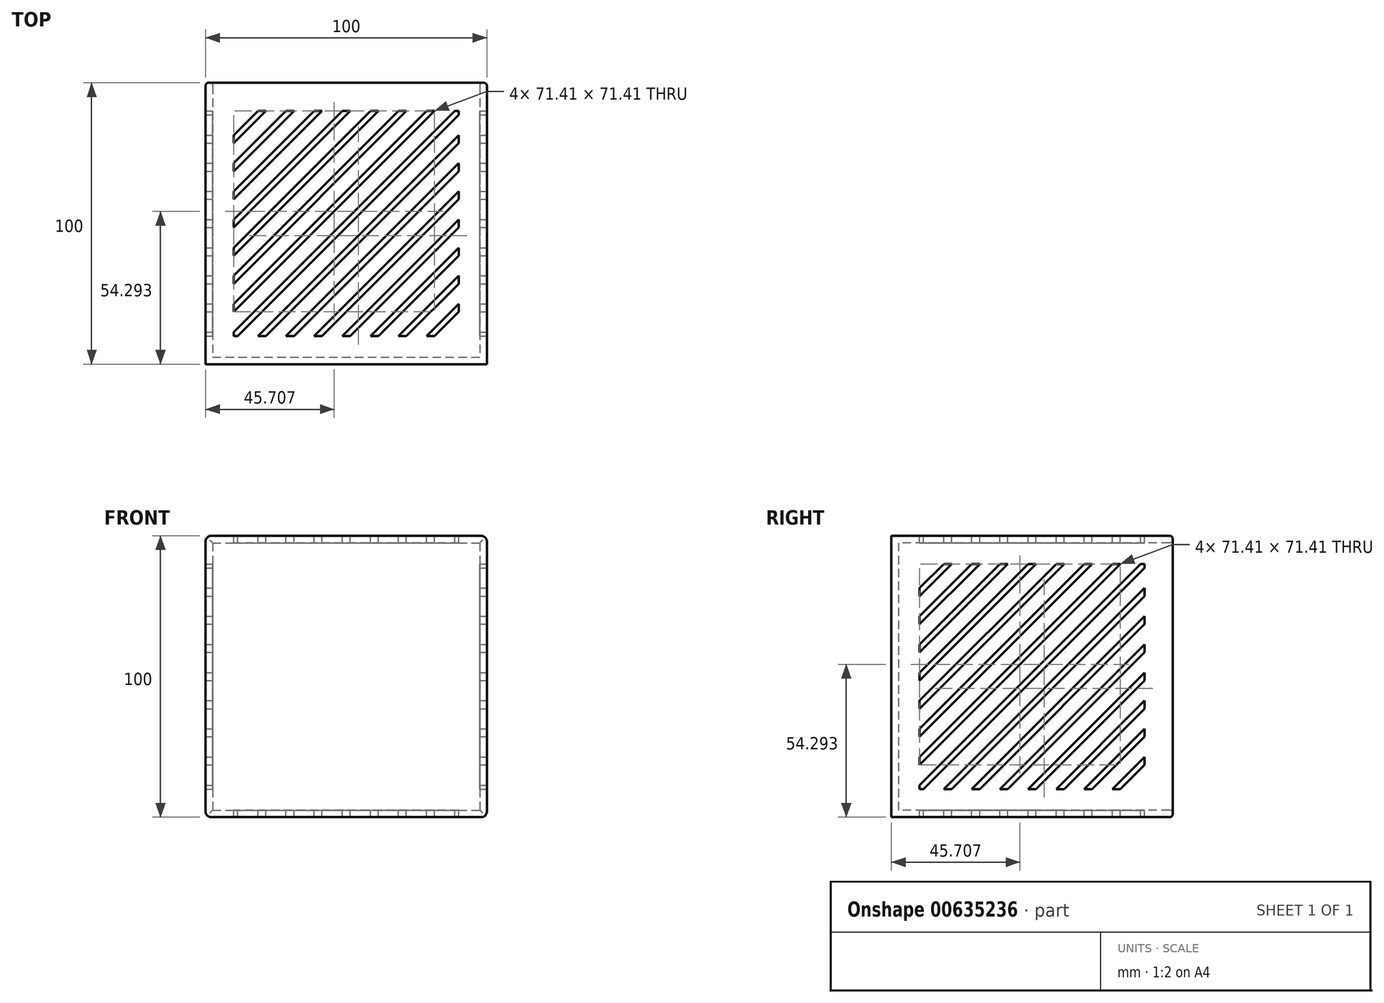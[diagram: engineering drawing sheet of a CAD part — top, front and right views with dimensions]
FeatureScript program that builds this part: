
annotation { "Feature Type Name" : "Feature", "Feature Type Description" : "" }
export const myFeature = defineFeature(function(context is Context, id is Id, definition is map)
    precondition{}
    {
        {
            var Q0;
            Q0=qCreatedBy(makeId("Top.planeOp"),FACE);
            var sketch = newSketch(context, id + "F0", { "sketchPlane" : qUnion([Q0])});
            skLineSegment(sketch, "E0.bottom", {"start": v(-50, 50) * mm, "end": v(50, 50) * mm});
            skLineSegment(sketch, "E0.top", {"start": v(-50, -50) * mm, "end": v(50, -50) * mm});
            skLineSegment(sketch, "E0.left", {"start": v(-50, 50) * mm, "end": v(-50, -50) * mm});
            skLineSegment(sketch, "E0.right", {"start": v(50, 50) * mm, "end": v(50, -50) * mm});
            skLineSegment(sketch, "E1", {"start": v(-30, 50) * mm, "end": v(-30, -50) * mm, "construction": true});
            skLineSegment(sketch, "E2", {"start": v(-20, 50) * mm, "end": v(-20, -50) * mm, "construction": true});
            skLineSegment(sketch, "E3", {"start": v(-10, 50) * mm, "end": v(-10, -50) * mm, "construction": true});
            skLineSegment(sketch, "E4", {"start": v(10, 50) * mm, "end": v(10, -50) * mm, "construction": true});
            skLineSegment(sketch, "E5", {"start": v(0, 50) * mm, "end": v(0, -50) * mm, "construction": true});
            skLineSegment(sketch, "E6", {"start": v(20, 50) * mm, "end": v(20, -50) * mm, "construction": true});
            skLineSegment(sketch, "E7", {"start": v(30, 50) * mm, "end": v(30, -50) * mm, "construction": true});
            skLineSegment(sketch, "E8", {"start": v(40, 50) * mm, "end": v(40, -50) * mm, "construction": true});
            skLineSegment(sketch, "E9", {"start": v(-40, 50) * mm, "end": v(-40, -50) * mm, "construction": true});
            skLineSegment(sketch, "E10", {"start": v(-50, 40) * mm, "end": v(50, 40) * mm, "construction": true});
            skLineSegment(sketch, "E11", {"start": v(-50, 30) * mm, "end": v(50, 30) * mm, "construction": true});
            skLineSegment(sketch, "E12", {"start": v(-50, 20) * mm, "end": v(50, 20) * mm, "construction": true});
            skLineSegment(sketch, "E13", {"start": v(-50, 10) * mm, "end": v(50, 10) * mm, "construction": true});
            skLineSegment(sketch, "E14", {"start": v(-50, -40) * mm, "end": v(50, -40) * mm, "construction": true});
            skLineSegment(sketch, "E15", {"start": v(50, -30) * mm, "end": v(-50, -30) * mm, "construction": true});
            skLineSegment(sketch, "E16", {"start": v(-50, -20) * mm, "end": v(50, -20) * mm, "construction": true});
            skLineSegment(sketch, "E17", {"start": v(-50, -10) * mm, "end": v(50, -10) * mm, "construction": true});
            skLineSegment(sketch, "E18", {"start": v(-50, 0) * mm, "end": v(50, 0) * mm, "construction": true});
            skSolve(sketch);
        }
        {
            var Q0;
            Q0=makeQuery(id+"F0.imprint","IMPRINT",FACE,{"disambiguationData":[TD([[makeQuery(id+"F0.imprint","IMPRINT",EDGE,{"derivedFrom":sQuery(id+"F0.wireOp",EDGE,"E0.bottom")}),-1.0]])]});
            extrude(context, id + "F1", {"entities" : qUnion([Q0]), "depth" : 100 * mm, "offsetDistance" : 25 * mm});
        }
        {
            var Q0;
            Q0=makeQuery(id+"F1.opExtrude","CAP_FACE",FACE,{"disambiguationData":[OSD([sQuery(id+"F0.wireOp",EDGE,"E0.bottom"),sQuery(id+"F0.wireOp",EDGE,"E0.top"),sQuery(id+"F0.wireOp",EDGE,"E0.left"),sQuery(id+"F0.wireOp",EDGE,"E0.right")])],"isStart":false});
            var sketch = newSketch(context, id + "F2", { "sketchPlane" : qUnion([Q0])});
            skLineSegment(sketch, "E19.bottom", {"start": v(-50, 50) * mm, "end": v(50, 50) * mm});
            skLineSegment(sketch, "E19.top", {"start": v(-50, -50) * mm, "end": v(50, -50) * mm});
            skLineSegment(sketch, "E19.left", {"start": v(-50, 50) * mm, "end": v(-50, -50) * mm});
            skLineSegment(sketch, "E19.right", {"start": v(50, 50) * mm, "end": v(50, -50) * mm});
            skLineSegment(sketch, "E20", {"start": v(40, 40) * mm, "end": v(40, -40) * mm});
            skLineSegment(sketch, "E21", {"start": v(-40, 40) * mm, "end": v(-40, -40) * mm});
            skLineSegment(sketch, "E22", {"start": v(-40, 40) * mm, "end": v(40, 40) * mm});
            skLineSegment(sketch, "E23", {"start": v(-40, -40) * mm, "end": v(40, -40) * mm});
            skLineSegment(sketch, "E24", {"start": v(-40, 31.41) * mm, "end": v(-31.41, 40) * mm});
            skLineSegment(sketch, "E25", {"start": v(-40, 21.41) * mm, "end": v(-21.41, 40) * mm});
            skLineSegment(sketch, "E26", {"start": v(-40, 11.41) * mm, "end": v(-11.41, 40) * mm});
            skLineSegment(sketch, "E27", {"start": v(-40, 28.59) * mm, "end": v(-28.59, 40) * mm});
            skLineSegment(sketch, "E28", {"start": v(-40, 18.59) * mm, "end": v(-18.59, 40) * mm});
            skLineSegment(sketch, "E29", {"start": v(-40, 8.59) * mm, "end": v(-8.59, 40) * mm});
            skLineSegment(sketch, "E30", {"start": v(-40, 1.41) * mm, "end": v(-1.41, 40) * mm});
            skLineSegment(sketch, "E31", {"start": v(-40, -1.41) * mm, "end": v(1.41, 40) * mm});
            skLineSegment(sketch, "E32", {"start": v(-40, -8.59) * mm, "end": v(8.59, 40) * mm});
            skLineSegment(sketch, "E33", {"start": v(-40, -11.41) * mm, "end": v(11.41, 40) * mm});
            skLineSegment(sketch, "E34", {"start": v(-40, -18.59) * mm, "end": v(18.59, 40) * mm});
            skLineSegment(sketch, "E35", {"start": v(-40, -21.41) * mm, "end": v(21.41, 40) * mm});
            skLineSegment(sketch, "E36", {"start": v(-40, -28.59) * mm, "end": v(28.59, 40) * mm});
            skLineSegment(sketch, "E37", {"start": v(31.41, 40) * mm, "end": v(-40, -31.41) * mm});
            skLineSegment(sketch, "E38", {"start": v(-40, -38.59) * mm, "end": v(38.59, 40) * mm});
            skLineSegment(sketch, "E39", {"start": v(-38.59, -40) * mm, "end": v(40, 38.59) * mm});
            skLineSegment(sketch, "E40", {"start": v(-31.41, -40) * mm, "end": v(40, 31.41) * mm});
            skLineSegment(sketch, "E41", {"start": v(-28.59, -40) * mm, "end": v(40, 28.59) * mm});
            skLineSegment(sketch, "E42", {"start": v(-21.41, -40) * mm, "end": v(40, 21.41) * mm});
            skLineSegment(sketch, "E43", {"start": v(-18.59, -40) * mm, "end": v(40, 18.59) * mm});
            skLineSegment(sketch, "E44", {"start": v(-11.41, -40) * mm, "end": v(40, 11.41) * mm});
            skLineSegment(sketch, "E45", {"start": v(40, 8.59) * mm, "end": v(-8.59, -40) * mm});
            skLineSegment(sketch, "E46", {"start": v(-1.41, -40) * mm, "end": v(40, 1.41) * mm});
            skLineSegment(sketch, "E47", {"start": v(40, -1.41) * mm, "end": v(1.41, -40) * mm});
            skLineSegment(sketch, "E48", {"start": v(11.41, -40) * mm, "end": v(40, -11.41) * mm});
            skLineSegment(sketch, "E49", {"start": v(8.59, -40) * mm, "end": v(40, -8.59) * mm});
            skLineSegment(sketch, "E50", {"start": v(18.59, -40) * mm, "end": v(40, -18.59) * mm});
            skLineSegment(sketch, "E51", {"start": v(21.41, -40) * mm, "end": v(40, -21.41) * mm});
            skLineSegment(sketch, "E52", {"start": v(31.41, -40) * mm, "end": v(40, -31.41) * mm});
            skLineSegment(sketch, "E53", {"start": v(40, -28.59) * mm, "end": v(28.59, -40) * mm});
            skPoint(sketch, "E54.orphan", {"position": v(-50, 40) * mm});
            skPoint(sketch, "E55.orphan", {"position": v(-40, 50) * mm});
            skPoint(sketch, "E56.orphan", {"position": v(-50, 0) * mm});
            skPoint(sketch, "E57.orphan", {"position": v(-50, -40) * mm});
            skPoint(sketch, "E58.orphan", {"position": v(-40, -50) * mm});
            skPoint(sketch, "E59.orphan", {"position": v(40, -50) * mm});
            skPoint(sketch, "E60.orphan", {"position": v(50, -40) * mm});
            skPoint(sketch, "E61.orphan", {"position": v(50, 40) * mm});
            skPoint(sketch, "E62.orphan", {"position": v(40, 50) * mm});
            skSolve(sketch);
        }
        {
            var Q0;
            Q0=makeQuery(id+"F1.opExtrude","SWEPT_FACE",FACE,{"disambiguationData":[OSD([sQuery(id+"F0.wireOp",EDGE,"E0.bottom")])]});
            shell(context, id + "F3", {"entities" : qUnion([Q0]), "thickness" : 2.5 * mm});
        }
        {
            var Q0;
            {var subQ0=sQuery(id+"F2.wireOp",EDGE,"E24");Q0=makeQuery(id+"F2.imprint","IMPRINT",FACE,{"disambiguationData":[TD([[makeQuery(id+"F2.imprint","IMPRINT",EDGE,{"derivedFrom":subQ0}),-1.0]])]});}
            var Q1;
            {var subQ0=sQuery(id+"F2.wireOp",EDGE,"E25");Q1=makeQuery(id+"F2.imprint","IMPRINT",FACE,{"disambiguationData":[TD([[makeQuery(id+"F2.imprint","IMPRINT",EDGE,{"derivedFrom":subQ0}),-1.0]])]});}
            var Q2;
            {var subQ0=sQuery(id+"F2.wireOp",EDGE,"E26");Q2=makeQuery(id+"F2.imprint","IMPRINT",FACE,{"disambiguationData":[TD([[makeQuery(id+"F2.imprint","IMPRINT",EDGE,{"derivedFrom":subQ0}),-1.0]])]});}
            var Q3;
            {var subQ0=sQuery(id+"F2.wireOp",EDGE,"E30");Q3=makeQuery(id+"F2.imprint","IMPRINT",FACE,{"disambiguationData":[TD([[makeQuery(id+"F2.imprint","IMPRINT",EDGE,{"derivedFrom":subQ0}),-1.0]])]});}
            var Q4;
            {var subQ0=sQuery(id+"F2.wireOp",EDGE,"E32");Q4=makeQuery(id+"F2.imprint","IMPRINT",FACE,{"disambiguationData":[TD([[makeQuery(id+"F2.imprint","IMPRINT",EDGE,{"derivedFrom":subQ0}),-1.0]])]});}
            var Q5;
            {var subQ0=sQuery(id+"F2.wireOp",EDGE,"E34");Q5=makeQuery(id+"F2.imprint","IMPRINT",FACE,{"disambiguationData":[TD([[makeQuery(id+"F2.imprint","IMPRINT",EDGE,{"derivedFrom":subQ0}),-1.0]])]});}
            var Q6;
            {var subQ0=sQuery(id+"F2.wireOp",EDGE,"E36");Q6=makeQuery(id+"F2.imprint","IMPRINT",FACE,{"disambiguationData":[TD([[makeQuery(id+"F2.imprint","IMPRINT",EDGE,{"derivedFrom":subQ0}),-1.0]])]});}
            var Q7;
            {var subQ7=sQuery(id+"F2.wireOp",EDGE,"E38");Q7=makeQuery(id+"F2.imprint","IMPRINT",FACE,{"disambiguationData":[TD([[makeQuery(id+"F2.imprint","IMPRINT",EDGE,{"derivedFrom":subQ7}),-1.0]])]});}
            var Q8;
            {var subQ0=sQuery(id+"F2.wireOp",EDGE,"E40");Q8=makeQuery(id+"F2.imprint","IMPRINT",FACE,{"disambiguationData":[TD([[makeQuery(id+"F2.imprint","IMPRINT",EDGE,{"derivedFrom":subQ0}),-1.0]])]});}
            var Q9;
            {var subQ0=sQuery(id+"F2.wireOp",EDGE,"E42");Q9=makeQuery(id+"F2.imprint","IMPRINT",FACE,{"disambiguationData":[TD([[makeQuery(id+"F2.imprint","IMPRINT",EDGE,{"derivedFrom":subQ0}),-1.0]])]});}
            var Q10;
            {var subQ0=sQuery(id+"F2.wireOp",EDGE,"E44");Q10=makeQuery(id+"F2.imprint","IMPRINT",FACE,{"disambiguationData":[TD([[makeQuery(id+"F2.imprint","IMPRINT",EDGE,{"derivedFrom":subQ0}),-1.0]])]});}
            var Q11;
            {var subQ0=sQuery(id+"F2.wireOp",EDGE,"E46");Q11=makeQuery(id+"F2.imprint","IMPRINT",FACE,{"disambiguationData":[TD([[makeQuery(id+"F2.imprint","IMPRINT",EDGE,{"derivedFrom":subQ0}),-1.0]])]});}
            var Q12;
            {var subQ0=sQuery(id+"F2.wireOp",EDGE,"E48");Q12=makeQuery(id+"F2.imprint","IMPRINT",FACE,{"disambiguationData":[TD([[makeQuery(id+"F2.imprint","IMPRINT",EDGE,{"derivedFrom":subQ0}),1.0]])]});}
            var Q13;
            {var subQ0=sQuery(id+"F2.wireOp",EDGE,"E50");Q13=makeQuery(id+"F2.imprint","IMPRINT",FACE,{"disambiguationData":[TD([[makeQuery(id+"F2.imprint","IMPRINT",EDGE,{"derivedFrom":subQ0}),-1.0]])]});}
            var Q14;
            {var subQ0=sQuery(id+"F2.wireOp",EDGE,"E52");Q14=makeQuery(id+"F2.imprint","IMPRINT",FACE,{"disambiguationData":[TD([[makeQuery(id+"F2.imprint","IMPRINT",EDGE,{"derivedFrom":subQ0}),1.0]])]});}
            extrude(context, id + "F4", {"entities" : qUnion([Q0, Q1, Q2, Q3, Q4, Q5, Q6, Q7, Q8, Q9, Q10, Q11, Q12, Q13, Q14]), "operationType" : NewBodyOperationType.REMOVE, "oppositeDirection" : true, "depth" : 102 * mm, "offsetDistance" : 25 * mm});
        }
        {
            var Q0;
            Q0=makeQuery(id+"F1.opExtrude","SWEPT_FACE",FACE,{"disambiguationData":[OSD([sQuery(id+"F0.wireOp",EDGE,"E0.right")])]});
            var sketch = newSketch(context, id + "F5", { "sketchPlane" : qUnion([Q0])});
            skLineSegment(sketch, "E63.bottom", {"start": v(-50, 100) * mm, "end": v(50, 100) * mm});
            skLineSegment(sketch, "E63.top", {"start": v(-50, 0) * mm, "end": v(50, 0) * mm});
            skLineSegment(sketch, "E63.left", {"start": v(-50, 100) * mm, "end": v(-50, 0) * mm});
            skLineSegment(sketch, "E63.right", {"start": v(50, 100) * mm, "end": v(50, 0) * mm});
            skLineSegment(sketch, "E64", {"start": v(-30, 100) * mm, "end": v(-30, 0) * mm, "construction": true});
            skLineSegment(sketch, "E65", {"start": v(-20, 100) * mm, "end": v(-20, 0) * mm, "construction": true});
            skLineSegment(sketch, "E66", {"start": v(-10, 100) * mm, "end": v(-10, 0) * mm, "construction": true});
            skLineSegment(sketch, "E67", {"start": v(10, 100) * mm, "end": v(10, 0) * mm, "construction": true});
            skLineSegment(sketch, "E68", {"start": v(0, 100) * mm, "end": v(0, 0) * mm, "construction": true});
            skLineSegment(sketch, "E69", {"start": v(20, 100) * mm, "end": v(20, 0) * mm, "construction": true});
            skLineSegment(sketch, "E70", {"start": v(30, 100) * mm, "end": v(30, 0) * mm, "construction": true});
            skLineSegment(sketch, "E71", {"start": v(40, 100) * mm, "end": v(40, 0) * mm});
            skLineSegment(sketch, "E72", {"start": v(-40, 90) * mm, "end": v(-40, 0) * mm});
            skLineSegment(sketch, "E73", {"start": v(-40, 90) * mm, "end": v(50, 90) * mm});
            skLineSegment(sketch, "E74", {"start": v(-50, 80) * mm, "end": v(50, 80) * mm, "construction": true});
            skLineSegment(sketch, "E75", {"start": v(-50, 70) * mm, "end": v(50, 70) * mm, "construction": true});
            skLineSegment(sketch, "E76", {"start": v(-50, 60) * mm, "end": v(50, 60) * mm, "construction": true});
            skLineSegment(sketch, "E77", {"start": v(-50, 10) * mm, "end": v(50, 10) * mm});
            skLineSegment(sketch, "E78", {"start": v(50, 20) * mm, "end": v(-50, 20) * mm, "construction": true});
            skLineSegment(sketch, "E79", {"start": v(-50, 30) * mm, "end": v(50, 30) * mm, "construction": true});
            skLineSegment(sketch, "E80", {"start": v(-50, 40) * mm, "end": v(50, 40) * mm, "construction": true});
            skLineSegment(sketch, "E81", {"start": v(-50, 50) * mm, "end": v(50, 50) * mm, "construction": true});
            skLineSegment(sketch, "E82", {"start": v(-40, 81.41) * mm, "end": v(-31.41, 90) * mm});
            skLineSegment(sketch, "E83", {"start": v(-40, 71.41) * mm, "end": v(-21.41, 90) * mm});
            skLineSegment(sketch, "E84", {"start": v(-40, 61.41) * mm, "end": v(-11.41, 90) * mm});
            skLineSegment(sketch, "E85", {"start": v(-40, 78.59) * mm, "end": v(-28.59, 90) * mm});
            skLineSegment(sketch, "E86", {"start": v(-40, 68.59) * mm, "end": v(-18.59, 90) * mm});
            skLineSegment(sketch, "E87", {"start": v(-40, 58.59) * mm, "end": v(-8.59, 90) * mm});
            skLineSegment(sketch, "E88", {"start": v(-40, 51.41) * mm, "end": v(-1.41, 90) * mm});
            skLineSegment(sketch, "E89", {"start": v(-40, 48.59) * mm, "end": v(1.41, 90) * mm});
            skLineSegment(sketch, "E90", {"start": v(-40, 41.41) * mm, "end": v(8.59, 90) * mm});
            skLineSegment(sketch, "E91", {"start": v(-40, 38.59) * mm, "end": v(11.41, 90) * mm});
            skLineSegment(sketch, "E92", {"start": v(-40, 31.41) * mm, "end": v(18.59, 90) * mm});
            skLineSegment(sketch, "E93", {"start": v(-40, 28.59) * mm, "end": v(21.41, 90) * mm});
            skLineSegment(sketch, "E94", {"start": v(-40, 21.41) * mm, "end": v(28.59, 90) * mm});
            skLineSegment(sketch, "E95", {"start": v(31.41, 90) * mm, "end": v(-40, 18.59) * mm});
            skLineSegment(sketch, "E96", {"start": v(-40, 11.41) * mm, "end": v(38.59, 90) * mm});
            skLineSegment(sketch, "E97", {"start": v(-38.59, 10) * mm, "end": v(40, 88.59) * mm});
            skLineSegment(sketch, "E98", {"start": v(-31.41, 10) * mm, "end": v(40, 81.41) * mm});
            skLineSegment(sketch, "E99", {"start": v(-28.59, 10) * mm, "end": v(40, 78.59) * mm});
            skLineSegment(sketch, "E100", {"start": v(-21.41, 10) * mm, "end": v(40, 71.41) * mm});
            skLineSegment(sketch, "E101", {"start": v(-18.59, 10) * mm, "end": v(40, 68.59) * mm});
            skLineSegment(sketch, "E102", {"start": v(-11.41, 10) * mm, "end": v(40, 61.41) * mm});
            skLineSegment(sketch, "E103", {"start": v(40, 58.59) * mm, "end": v(-8.59, 10) * mm});
            skLineSegment(sketch, "E104", {"start": v(-1.41, 10) * mm, "end": v(40, 51.41) * mm});
            skLineSegment(sketch, "E105", {"start": v(40, 48.59) * mm, "end": v(1.41, 10) * mm});
            skLineSegment(sketch, "E106", {"start": v(11.41, 10) * mm, "end": v(40, 38.59) * mm});
            skLineSegment(sketch, "E107", {"start": v(8.59, 10) * mm, "end": v(40, 41.41) * mm});
            skLineSegment(sketch, "E108", {"start": v(18.59, 10) * mm, "end": v(40, 31.41) * mm});
            skLineSegment(sketch, "E109", {"start": v(21.41, 10) * mm, "end": v(40, 28.59) * mm});
            skLineSegment(sketch, "E110", {"start": v(31.41, 10) * mm, "end": v(40, 18.59) * mm});
            skLineSegment(sketch, "E111", {"start": v(40, 21.41) * mm, "end": v(28.59, 10) * mm});
            skPoint(sketch, "E112.orphan", {"position": v(-50, 90) * mm});
            skPoint(sketch, "E113.orphan", {"position": v(-40, 100) * mm});
            skPoint(sketch, "E114.orphan", {"position": v(-40, 50) * mm});
            skPoint(sketch, "E115.end.orphan", {"position": v(0, 90) * mm});
            skPoint(sketch, "E116.orphan", {"position": v(0, 10) * mm});
            skPoint(sketch, "E117.end.orphan", {"position": v(40, 50) * mm});
            skSolve(sketch);
        }
        {
            var Q0;
            {var subQ0=sQuery(id+"F5.wireOp",EDGE,"E82");Q0=makeQuery(id+"F5.imprint","IMPRINT",FACE,{"disambiguationData":[TD([[makeQuery(id+"F5.imprint","IMPRINT",EDGE,{"derivedFrom":subQ0}),-1.0]])]});}
            var Q1;
            {var subQ0=sQuery(id+"F5.wireOp",EDGE,"E83");Q1=makeQuery(id+"F5.imprint","IMPRINT",FACE,{"disambiguationData":[TD([[makeQuery(id+"F5.imprint","IMPRINT",EDGE,{"derivedFrom":subQ0}),-1.0]])]});}
            var Q2;
            {var subQ0=sQuery(id+"F5.wireOp",EDGE,"E84");Q2=makeQuery(id+"F5.imprint","IMPRINT",FACE,{"disambiguationData":[TD([[makeQuery(id+"F5.imprint","IMPRINT",EDGE,{"derivedFrom":subQ0}),-1.0]])]});}
            var Q3;
            {var subQ0=sQuery(id+"F5.wireOp",EDGE,"E88");Q3=makeQuery(id+"F5.imprint","IMPRINT",FACE,{"disambiguationData":[TD([[makeQuery(id+"F5.imprint","IMPRINT",EDGE,{"derivedFrom":subQ0}),-1.0]])]});}
            var Q4;
            {var subQ0=sQuery(id+"F5.wireOp",EDGE,"E90");Q4=makeQuery(id+"F5.imprint","IMPRINT",FACE,{"disambiguationData":[TD([[makeQuery(id+"F5.imprint","IMPRINT",EDGE,{"derivedFrom":subQ0}),-1.0]])]});}
            var Q5;
            {var subQ0=sQuery(id+"F5.wireOp",EDGE,"E92");Q5=makeQuery(id+"F5.imprint","IMPRINT",FACE,{"disambiguationData":[TD([[makeQuery(id+"F5.imprint","IMPRINT",EDGE,{"derivedFrom":subQ0}),-1.0]])]});}
            var Q6;
            {var subQ0=sQuery(id+"F5.wireOp",EDGE,"E94");Q6=makeQuery(id+"F5.imprint","IMPRINT",FACE,{"disambiguationData":[TD([[makeQuery(id+"F5.imprint","IMPRINT",EDGE,{"derivedFrom":subQ0}),-1.0]])]});}
            var Q7;
            {var subQ0=sQuery(id+"F5.wireOp",EDGE,"E96");Q7=makeQuery(id+"F5.imprint","IMPRINT",FACE,{"disambiguationData":[TD([[makeQuery(id+"F5.imprint","IMPRINT",EDGE,{"derivedFrom":subQ0}),-1.0]])]});}
            var Q8;
            {var subQ0=sQuery(id+"F5.wireOp",EDGE,"E98");Q8=makeQuery(id+"F5.imprint","IMPRINT",FACE,{"disambiguationData":[TD([[makeQuery(id+"F5.imprint","IMPRINT",EDGE,{"derivedFrom":subQ0}),-1.0]])]});}
            var Q9;
            {var subQ0=sQuery(id+"F5.wireOp",EDGE,"E100");Q9=makeQuery(id+"F5.imprint","IMPRINT",FACE,{"disambiguationData":[TD([[makeQuery(id+"F5.imprint","IMPRINT",EDGE,{"derivedFrom":subQ0}),-1.0]])]});}
            var Q10;
            {var subQ0=sQuery(id+"F5.wireOp",EDGE,"E102");Q10=makeQuery(id+"F5.imprint","IMPRINT",FACE,{"disambiguationData":[TD([[makeQuery(id+"F5.imprint","IMPRINT",EDGE,{"derivedFrom":subQ0}),-1.0]])]});}
            var Q11;
            {var subQ0=sQuery(id+"F5.wireOp",EDGE,"E104");Q11=makeQuery(id+"F5.imprint","IMPRINT",FACE,{"disambiguationData":[TD([[makeQuery(id+"F5.imprint","IMPRINT",EDGE,{"derivedFrom":subQ0}),-1.0]])]});}
            var Q12;
            {var subQ0=sQuery(id+"F5.wireOp",EDGE,"E106");Q12=makeQuery(id+"F5.imprint","IMPRINT",FACE,{"disambiguationData":[TD([[makeQuery(id+"F5.imprint","IMPRINT",EDGE,{"derivedFrom":subQ0}),1.0]])]});}
            var Q13;
            {var subQ0=sQuery(id+"F5.wireOp",EDGE,"E108");Q13=makeQuery(id+"F5.imprint","IMPRINT",FACE,{"disambiguationData":[TD([[makeQuery(id+"F5.imprint","IMPRINT",EDGE,{"derivedFrom":subQ0}),-1.0]])]});}
            var Q14;
            {var subQ0=sQuery(id+"F5.wireOp",EDGE,"E110");Q14=makeQuery(id+"F5.imprint","IMPRINT",FACE,{"disambiguationData":[TD([[makeQuery(id+"F5.imprint","IMPRINT",EDGE,{"derivedFrom":subQ0}),1.0]])]});}
            extrude(context, id + "F6", {"entities" : qUnion([Q0, Q1, Q2, Q3, Q4, Q5, Q6, Q7, Q8, Q9, Q10, Q11, Q12, Q13, Q14]), "operationType" : NewBodyOperationType.REMOVE, "oppositeDirection" : true, "depth" : 108.7 * mm, "offsetDistance" : 25 * mm});
        }
        {
            var Q0;
            Q0=makeQuery(id+"F1.opExtrude","SWEPT_FACE",FACE,{"disambiguationData":[OSD([sQuery(id+"F0.wireOp",EDGE,"E0.bottom")])]});
            fillet(context, id + "F7", {"entities" : qUnion([Q0]), "radius" : 1 * mm, "tangentPropagation" : true, "allowEdgeOverflow" : false});
        }
        {
            var Q0;
            Q0=makeQuery(id+"F1.opExtrude","CAP_EDGE",EDGE,{"disambiguationData":[OSD([sQuery(id+"F0.wireOp",EDGE,"E0.right")])],"isStart":true});
            fillet(context, id + "F8", {"entities" : qUnion([Q0]), "radius" : 2 * mm, "tangentPropagation" : true, "allowEdgeOverflow" : false});
        }
        {
            var Q0;
            Q0=makeQuery(id+"F1.opExtrude","CAP_EDGE",EDGE,{"disambiguationData":[OSD([sQuery(id+"F0.wireOp",EDGE,"E0.left")])],"isStart":true});
            fillet(context, id + "F9", {"entities" : qUnion([Q0]), "radius" : 2 * mm, "tangentPropagation" : true, "allowEdgeOverflow" : false});
        }
        {
            var Q0;
            Q0=makeQuery(id+"F1.opExtrude","CAP_EDGE",EDGE,{"disambiguationData":[OSD([sQuery(id+"F0.wireOp",EDGE,"E0.left")])],"isStart":false});
            fillet(context, id + "F10", {"entities" : qUnion([Q0]), "radius" : 2 * mm, "tangentPropagation" : true, "allowEdgeOverflow" : false});
        }
        {
            var Q0;
            Q0=makeQuery(id+"F1.opExtrude","CAP_EDGE",EDGE,{"disambiguationData":[OSD([sQuery(id+"F0.wireOp",EDGE,"E0.right")])],"isStart":false});
            fillet(context, id + "F11", {"entities" : qUnion([Q0]), "radius" : 2 * mm, "tangentPropagation" : true, "allowEdgeOverflow" : false});
        }
    });
